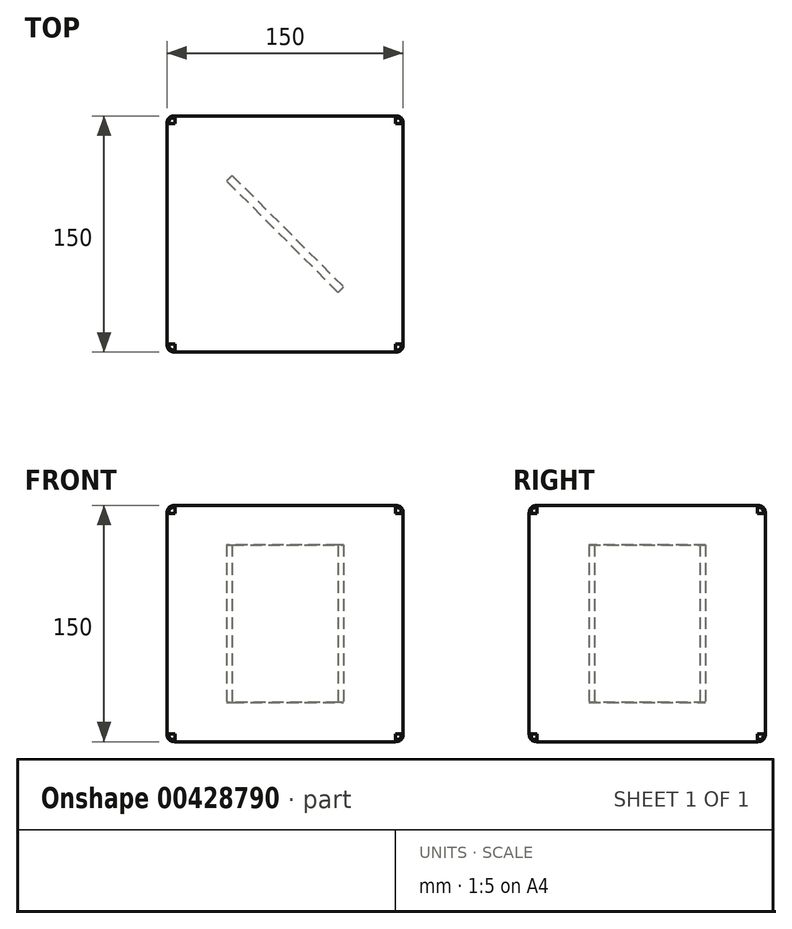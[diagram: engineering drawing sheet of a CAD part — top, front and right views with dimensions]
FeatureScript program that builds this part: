
annotation { "Feature Type Name" : "Feature", "Feature Type Description" : "" }
export const myFeature = defineFeature(function(context is Context, id is Id, definition is map)
    precondition{}
    {
        {
            var Q0;
            Q0=qCreatedBy(makeId("Top.planeOp"),FACE);
            var sketch = newSketch(context, id + "F0", { "sketchPlane" : qUnion([Q0])});
            skLineSegment(sketch, "E0.bottom", {"start": v(75, 75) * mm, "end": v(-75, 75) * mm});
            skLineSegment(sketch, "E0.top", {"start": v(75, -75) * mm, "end": v(-75, -75) * mm});
            skLineSegment(sketch, "E0.left", {"start": v(75, 75) * mm, "end": v(75, -75) * mm});
            skLineSegment(sketch, "E0.right", {"start": v(-75, 75) * mm, "end": v(-75, -75) * mm});
            skPoint(sketch, "E1.middle", {"position": v(0, 0) * mm});
            skSolve(sketch);
        }
        {
            var Q0;
            Q0=qSketchRegion(id+"F0",true);
            extrude(context, id + "F1", {"entities" : qUnion([Q0]), "depth" : 150 * mm});
        }
        {
            var Q0;
            Q0=makeQuery(id+"F1.opExtrude","SWEPT_EDGE",EDGE,{"disambiguationData":[OSD([sQuery(id+"F0.wireOp",EDGE,"E0.top"),sQuery(id+"F0.wireOp",EDGE,"E0.left")])]});
            var Q1;
            Q1=makeQuery(id+"F1.opExtrude","SWEPT_EDGE",EDGE,{"disambiguationData":[OSD([sQuery(id+"F0.wireOp",EDGE,"E0.top"),sQuery(id+"F0.wireOp",EDGE,"E0.right")])]});
            var Q2;
            Q2=makeQuery(id+"F1.opExtrude","SWEPT_EDGE",EDGE,{"disambiguationData":[OSD([sQuery(id+"F0.wireOp",EDGE,"E0.bottom"),sQuery(id+"F0.wireOp",EDGE,"E0.right")])]});
            var Q3;
            Q3=makeQuery(id+"F1.opExtrude","SWEPT_EDGE",EDGE,{"disambiguationData":[OSD([sQuery(id+"F0.wireOp",EDGE,"E0.bottom"),sQuery(id+"F0.wireOp",EDGE,"E0.left")])]});
            var Q4;
            Q4=makeQuery(id+"F1.opExtrude","CAP_EDGE",EDGE,{"disambiguationData":[OSD([sQuery(id+"F0.wireOp",EDGE,"E0.right")])],"isStart":false});
            var Q5;
            Q5=makeQuery(id+"F1.opExtrude","CAP_EDGE",EDGE,{"disambiguationData":[OSD([sQuery(id+"F0.wireOp",EDGE,"E0.bottom")])],"isStart":false});
            var Q6;
            Q6=makeQuery(id+"F1.opExtrude","CAP_EDGE",EDGE,{"disambiguationData":[OSD([sQuery(id+"F0.wireOp",EDGE,"E0.left")])],"isStart":false});
            var Q7;
            Q7=makeQuery(id+"F1.opExtrude","CAP_EDGE",EDGE,{"disambiguationData":[OSD([sQuery(id+"F0.wireOp",EDGE,"E0.top")])],"isStart":false});
            var Q8;
            Q8=makeQuery(id+"F1.opExtrude","CAP_EDGE",EDGE,{"disambiguationData":[OSD([sQuery(id+"F0.wireOp",EDGE,"E0.top")])],"isStart":true});
            var Q9;
            Q9=makeQuery(id+"F1.opExtrude","CAP_EDGE",EDGE,{"disambiguationData":[OSD([sQuery(id+"F0.wireOp",EDGE,"E0.left")])],"isStart":true});
            var Q10;
            Q10=makeQuery(id+"F1.opExtrude","CAP_EDGE",EDGE,{"disambiguationData":[OSD([sQuery(id+"F0.wireOp",EDGE,"E0.right")])],"isStart":true});
            var Q11;
            Q11=makeQuery(id+"F1.opExtrude","CAP_EDGE",EDGE,{"disambiguationData":[OSD([sQuery(id+"F0.wireOp",EDGE,"E0.bottom")])],"isStart":true});
            fillet(context, id + "F2", {"entities" : qUnion([Q0, Q1, Q2, Q3, Q4, Q5, Q6, Q7, Q8, Q9, Q10, Q11]), "radius" : 5 * mm, "tangentPropagation" : true, "rho" : 0.5, "crossSection" : FilletCrossSection.CONIC, "allowEdgeOverflow" : false});
        }
        {
            var Q0;
            Q0=makeQuery(id+"F1.opExtrude","CAP_FACE",FACE,{"disambiguationData":[OSD([sQuery(id+"F0.wireOp",EDGE,"E0.bottom"),sQuery(id+"F0.wireOp",EDGE,"E0.top"),sQuery(id+"F0.wireOp",EDGE,"E0.left"),sQuery(id+"F0.wireOp",EDGE,"E0.right")])],"isStart":true});
            var sketch = newSketch(context, id + "F3", { "sketchPlane" : qUnion([Q0])});
            skLineSegment(sketch, "E2", {"start": v(-37.12, -33.59) * mm, "end": v(-33.59, -37.12) * mm});
            skLineSegment(sketch, "E3", {"start": v(-33.59, -37.12) * mm, "end": v(37.12, 33.59) * mm});
            skLineSegment(sketch, "E4", {"start": v(37.12, 33.59) * mm, "end": v(33.59, 37.12) * mm});
            skLineSegment(sketch, "E5", {"start": v(33.59, 37.12) * mm, "end": v(-37.12, -33.59) * mm});
            skLineSegment(sketch, "E6", {"start": v(35.36, 35.36) * mm, "end": v(-35.36, -35.36) * mm, "construction": true});
            skLineSegment(sketch, "E7", {"start": v(-1.77, 1.77) * mm, "end": v(1.77, -1.77) * mm, "construction": true});
            skLineSegment(sketch, "E8", {"start": v(-75, -75) * mm, "end": v(75, 75) * mm, "construction": true});
            skLineSegment(sketch, "E9", {"start": v(-75, 75) * mm, "end": v(75, -75) * mm, "construction": true});
            skSolve(sketch);
        }
        {
            var Q0;
            Q0=qSketchRegion(id+"F3",true);
            extrude(context, id + "F4", {"entities" : qUnion([Q0]), "oppositeDirection" : true, "depth" : 125 * mm, "hasSecondDirection" : true, "secondDirectionOppositeDirection" : true, "secondDirectionDepth" : 25 * mm});
        }
    });
